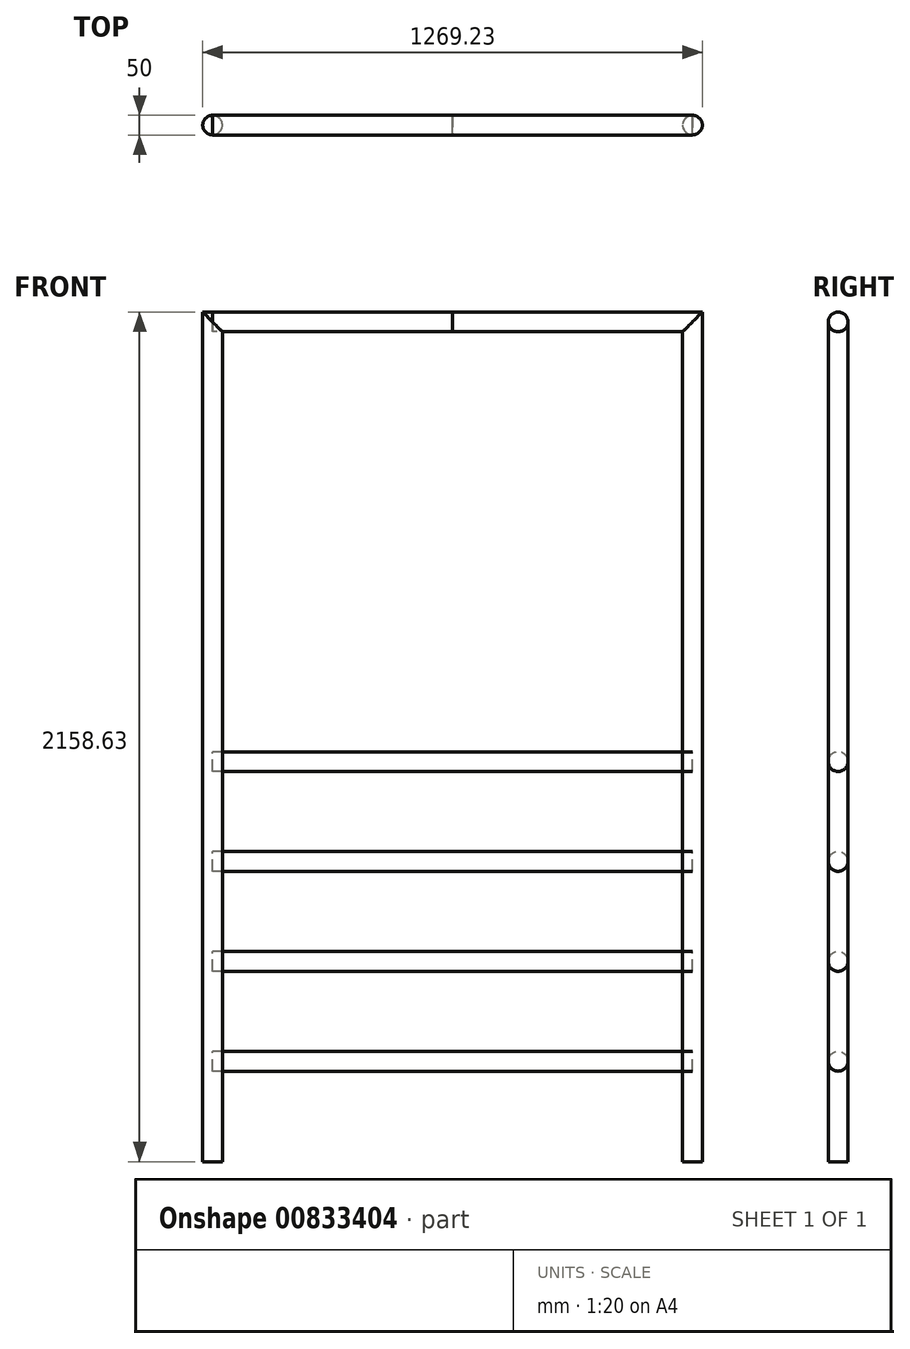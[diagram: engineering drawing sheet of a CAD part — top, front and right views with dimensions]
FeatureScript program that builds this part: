
annotation { "Feature Type Name" : "Feature", "Feature Type Description" : "" }
export const myFeature = defineFeature(function(context is Context, id is Id, definition is map)
    precondition{}
    {
        {
            var Q0;
            Q0=qCreatedBy(makeId("Top.planeOp"),FACE);
            var sketch = newSketch(context, id + "F0", { "sketchPlane" : qUnion([Q0])});
            skCircle(sketch, "E0", {"center": v(0, 0) * mm, "radius": 25 * mm});
            skSolve(sketch);
        }
        {
            var Q0;
            Q0=qCreatedBy(makeId("Front.planeOp"),FACE);
            var sketch = newSketch(context, id + "F1", { "sketchPlane" : qUnion([Q0])});
            skLineSegment(sketch, "E1", {"start": v(0, 0) * mm, "end": v(0, 2133.6) * mm});
            skLineSegment(sketch, "E2", {"start": v(0, 2133.6) * mm, "end": v(1219.2, 2133.6) * mm});
            skLineSegment(sketch, "E3", {"start": v(1219.2, 2133.6) * mm, "end": v(1219.2, 0) * mm});
            skLineSegment(sketch, "E4", {"start": v(0, 2133.6) * mm, "end": v(609.6, 2133.6) * mm});
            skLineSegment(sketch, "E5", {"start": v(0, 0) * mm, "end": v(0, 254) * mm});
            skLineSegment(sketch, "E6", {"start": v(0, 254) * mm, "end": v(0, 508) * mm});
            skLineSegment(sketch, "E7", {"start": v(0, 508) * mm, "end": v(0, 762) * mm});
            skLineSegment(sketch, "E8", {"start": v(0, 762) * mm, "end": v(0, 1016) * mm});
            skLineSegment(sketch, "E9", {"start": v(0, 1016) * mm, "end": v(1219.2, 1016) * mm});
            skLineSegment(sketch, "E10", {"start": v(0, 762) * mm, "end": v(1219.2, 762) * mm});
            skLineSegment(sketch, "E11", {"start": v(0, 508) * mm, "end": v(1219.2, 508) * mm});
            skLineSegment(sketch, "E12", {"start": v(0, 254) * mm, "end": v(1219.2, 254) * mm});
            skSolve(sketch);
        }
        {
            var Q0;
            Q0=makeQuery(id+"F0.imprint","IMPRINT",FACE,{"disambiguationData":[TD([[makeQuery(id+"F0.imprint","IMPRINT",EDGE,{"derivedFrom":sQuery(id+"F0.wireOp",EDGE,"E0")}),1.0]])]});
            var Q1;
            Q1=sQuery(id+"F1.wireOp",EDGE,"E1");
            var Q2;
            Q2=sQuery(id+"F1.wireOp",EDGE,"E4");
            sweep(context, id + "F2", {"profiles" : qUnion([Q0]), "path" : qUnion([Q1, Q2])});
        }
        {
            var Q0;
            Q0=sQuery(id+"F1.wireOp",VERTEX,"E3.end");
            var Q1;
            Q1=sQuery(id+"F1.wireOp",EDGE,"E3");
            cPlane(context, id + "F3", {"entities" : qUnion([Q0, Q1]), "cplaneType" : CPlaneType.LINE_POINT, "offset" : 25.4 * mm, "width" : 152.4 * mm, "height" : 152.4 * mm});
        }
        {
            var Q0;
            Q0=qCreatedBy(id+"F3.planeOp",FACE);
            var sketch = newSketch(context, id + "F4", { "sketchPlane" : qUnion([Q0])});
            skPoint(sketch, "E13", {"position": v(1219.23, 0) * mm});
            skCircle(sketch, "E14", {"center": v(1219.23, 0) * mm, "radius": 25 * mm});
            skSolve(sketch);
        }
        {
            var Q0;
            Q0=makeQuery(id+"F4.imprint","IMPRINT",FACE,{"disambiguationData":[TD([[makeQuery(id+"F4.imprint","IMPRINT",EDGE,{"derivedFrom":sQuery(id+"F4.wireOp",EDGE,"E14")}),1.0]])]});
            var Q1;
            Q1=sQuery(id+"F1.wireOp",EDGE,"E3");
            var Q2;
            Q2=sQuery(id+"F1.wireOp",EDGE,"E2");
            sweep(context, id + "F5", {"profiles" : qUnion([Q0]), "path" : qUnion([Q1, Q2])});
        }
        {
            var Q0;
            Q0=sQuery(id+"F1.wireOp",VERTEX,"E8.end");
            var Q1;
            Q1=sQuery(id+"F1.wireOp",EDGE,"E9");
            cPlane(context, id + "F6", {"entities" : qUnion([Q0, Q1]), "cplaneType" : CPlaneType.LINE_POINT, "offset" : 25.4 * mm, "width" : 152.4 * mm, "height" : 152.4 * mm});
        }
        {
            var Q0;
            Q0=qCreatedBy(id+"F6.planeOp",FACE);
            var sketch = newSketch(context, id + "F7", { "sketchPlane" : qUnion([Q0])});
            skCircle(sketch, "E15", {"center": v(0, 1016.33) * mm, "radius": 25 * mm});
            skCircle(sketch, "E16", {"center": v(0, 762.7) * mm, "radius": 25 * mm});
            skCircle(sketch, "E17", {"center": v(0, 508.56) * mm, "radius": 25 * mm});
            skCircle(sketch, "E18", {"center": v(0, 254.9) * mm, "radius": 25 * mm});
            skSolve(sketch);
        }
        {
            var Q0;
            Q0 = qSketchRegion(id + "F7", true);
            extrude(context, id + "F8", {"entities" : qUnion([Q0]), "depth" : 1219.2 * mm, "offsetDistance" : 25.4 * mm});
        }
    });
